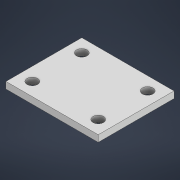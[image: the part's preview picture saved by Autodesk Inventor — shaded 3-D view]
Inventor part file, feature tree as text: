
AUTODESK INVENTOR PART (.ipt)
format: ipt  version: 2021 (Build 250183000, 183)  size: 111,104 bytes
history: native  units: mm
features: extrude x2, sketch x2
ambient origin geometry x8: Origin, YZ Plane, XZ Plane, XY Plane, X Axis, Y Axis, Z Axis, Center Point
bodies: Volumenkörper1 (feature_tree)
feature tree (4):
  extrude  "Extrusion1"  Depth=23.0mm
  extrude  "Extrusion2"  Depth=2.0mm
  sketch  "Skizze1"  dims[d0=28.0mm d1=23.0mm]
  sketch  "Skizze2"  dims[d2=2.0mm d3=0.0mm d4=3.2mm d5=3.2mm d6=3.2mm d7=3.2mm d8=20.0mm d9=20.0mm d10=15.0mm d11=15.0mm d12=7.5mm d13=10.0mm d14=10.0mm d15=7.5mm d16=2.0mm d17=0.0mm]
